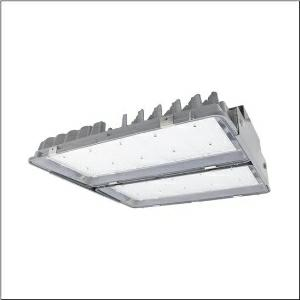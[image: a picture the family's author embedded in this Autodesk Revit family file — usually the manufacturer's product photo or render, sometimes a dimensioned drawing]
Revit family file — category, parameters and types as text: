
# Revit family: highbay_11xtreme_51hf82db4wma
name_source: partatom
category: Lighting Fixtures
units: mm (PartAtom-declared; Revit-internal decimal feet)

## family parameters
Cut with Voids When Loaded = No
Host = Face
Light Source = No
Part Type = Normal
Room Calculation Point = No
Round Connector Dimension = Use Diameter
Shared = No

## types (1)
- --- (1 x LED, 75000 lm, 422.2 W, 4000K)
    Apparent Load = 422 VA
    CIE Flux Codes = 84 96 100 100 100
    Color Rendering = 80
    Color Temperature = 4000K
    Default Elevation = 1800 mm
    Description = Highbay 11Xtreme, high bay luminaire, primary light control with lens, of PMMA, primary optical cover: cover, of toughened safety glass, light emission: direct distribution, primary light characteristic: symmetric, installation type: suspended mounting, surface-mounted, 2x LED module,for 1x 2x LED, rated luminous flux: 75.000lm, luminous efficacy: 178lm/W, light colour: 840, colour temperature: 4000K, control gear: DALI 2 (with two DALI addresses), with cable H07RN-F 5x 1.5mm², mains connection: 220..240V, AC, 50/60Hz, cable length: 1,5m, rated input power: 422W, luminaire housing, of diecast aluminium, partly coated, silver, length: 595mm, width: 560mm, height: 195mm, protection rating (complete): IP66, insulation class (complete): insulation class I (protective earthing), certification: CE, ENEC, UKCA, protection symbol: D, ball protection: ball impact resistant according to DIN VDE 0710 part 13 (with chain suspension), impact resistance: IK08, permissible operating ambient temperature: -25..+45°C, reducing of maximum allowable ambient temperature of 5°C with ceiling mounting, packaging unit: 1 piece
    Height = 157 mm
    Lamp = 1 x LED
    Lamp Light Flux = 75000 lm
    Lamp Power = 422.2 W
    Lamp count = 1
    Length = 593 mm
    Luminous efficacy = 178 lm/W
    Manufacturer = Siteco
    ModVariant = No
    Model = 51HF82DB4WMA
    Mounting Place = Ceiling
    Mounting Type = Pendant
    Number of Poles = 1
    OnlyDefault = Yes
    Power Factor = 1
    Product Name = Highbay 11Xtreme
    Product group = high bay luminaire
    ProductGroupID = 901
    Protection Class = Protection class I
    Protection Degree = IP 66
    RLX_Detail_Level = 1
    RLX_Emergency_Light_Flux = 0 lm
    RLX_Emergency_Type = 0
    RLX_Emergency_Type_DB = No
    RlxData = <blob elided: 34361 chars, md5=22b2a1e9>
    Socket = socket
    Standby Power = 0 W
    System Light Flux = 75000 lm
    System Power = 422 W
    Type Comments = factory setting: luminous flux: 100 % | dim-lin: 254 | 1389 mA
    Type Image = l_1258340.jpg
    URL = http://relux.com
    VarID = @adj_104711
    Voltage = 0 V
    Weight = 0.00 kg
    Width = 568 mm

## geometry (parser evidence)
native form markers: Blend x4, Sweep x10
no freeform markers — native parametric forms only
